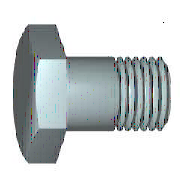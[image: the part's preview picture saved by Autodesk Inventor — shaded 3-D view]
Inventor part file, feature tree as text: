
AUTODESK INVENTOR PART (.ipt)
format: ipt  version: 2024 (Build 280153000, 153)  size: 189,440 bytes
history: native  units: mm (DEFAULTED — no unit token found)
features: extrude x1, chamfer x1, plane x1
ambient origin geometry x7: Origin, YZ Plane, XZ Plane, X Axis, Y Axis, Z Axis, Center Point
bodies: Solid1 (feature_tree), Body (feature_tree)
feature tree (3):
  extrude  "Head"  Depth=100.0mm
  chamfer  "Chamfer1"  Distance=30.0mm
  plane  "Work Plane1"
